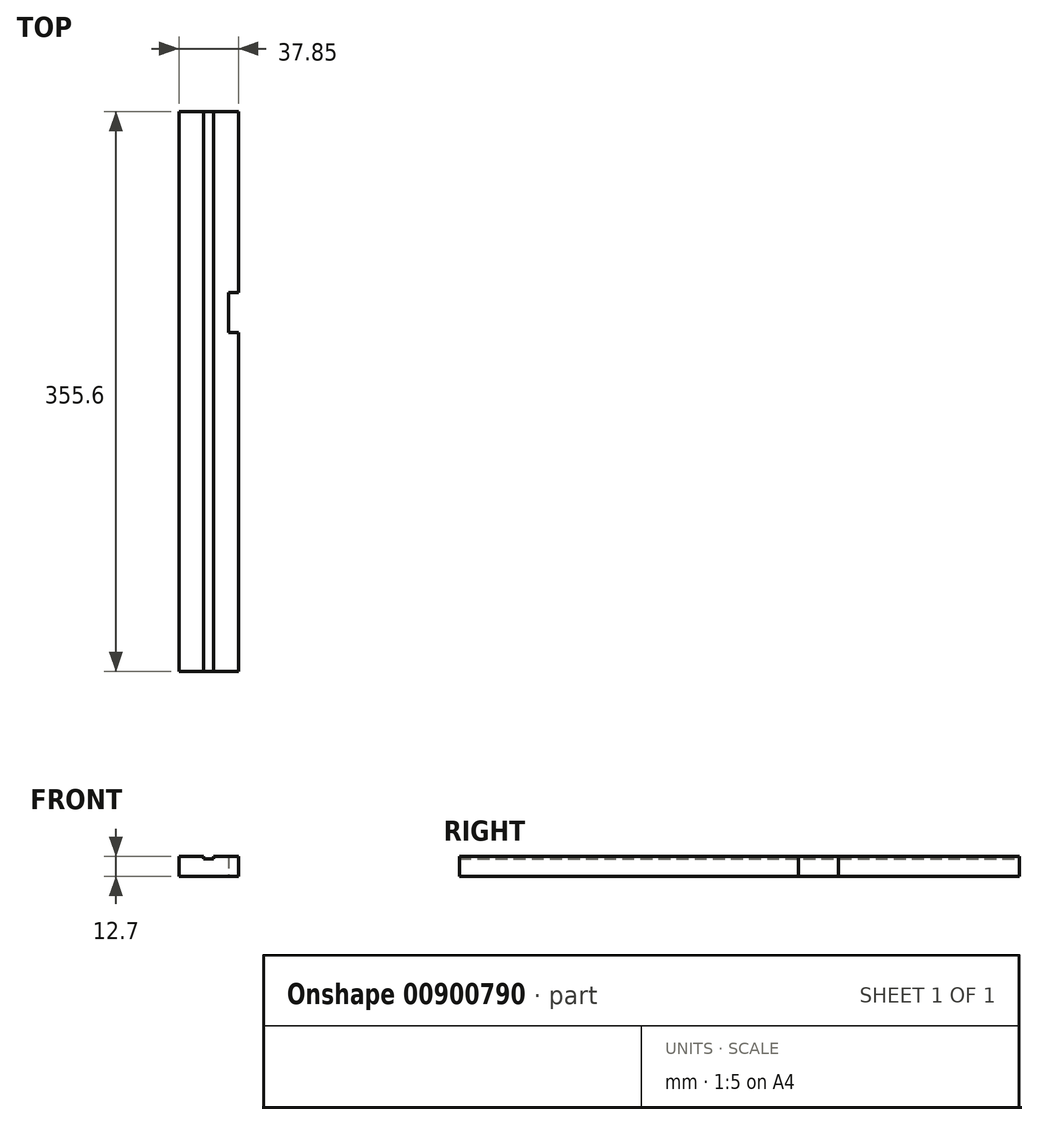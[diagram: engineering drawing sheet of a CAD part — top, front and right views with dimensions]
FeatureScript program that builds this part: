
annotation { "Feature Type Name" : "Feature", "Feature Type Description" : "" }
export const myFeature = defineFeature(function(context is Context, id is Id, definition is map)
    precondition{}
    {
        {
            var Q0;
            Q0=qCreatedBy(makeId("Front.planeOp"),FACE);
            var sketch = newSketch(context, id + "F0", { "sketchPlane" : qUnion([Q0])});
            skLineSegment(sketch, "E0.bottom", {"start": v(0, 12.7) * mm, "end": v(15.75, 12.7) * mm});
            skLineSegment(sketch, "E0.top", {"start": v(0, 0) * mm, "end": v(37.85, 0) * mm});
            skLineSegment(sketch, "E0.left", {"start": v(0, 12.7) * mm, "end": v(0, 0) * mm});
            skLineSegment(sketch, "E0.right", {"start": v(37.85, 12.7) * mm, "end": v(37.85, 0) * mm});
            skLineSegment(sketch, "E1.top", {"start": v(15.75, 11.18) * mm, "end": v(22.1, 11.18) * mm});
            skLineSegment(sketch, "E1.left", {"start": v(15.75, 12.7) * mm, "end": v(15.75, 11.18) * mm});
            skLineSegment(sketch, "E1.right", {"start": v(22.1, 12.7) * mm, "end": v(22.1, 11.18) * mm});
            skLineSegment(sketch, "E2.trimOffspring", {"start": v(22.1, 12.7) * mm, "end": v(37.85, 12.7) * mm});
            skSolve(sketch);
        }
        {
            var Q0;
            Q0=makeQuery(id+"F0.imprint","IMPRINT",FACE,{"disambiguationData":[TD([[makeQuery(id+"F0.imprint","IMPRINT",EDGE,{"derivedFrom":sQuery(id+"F0.wireOp",EDGE,"E0.bottom")}),-1.0]])]});
            extrude(context, id + "F1", {"entities" : qUnion([Q0]), "depth" : 355.6 * mm, "offsetDistance" : 25.4 * mm});
        }
        {
            var Q0;
            Q0=makeQuery(id+"F1.opExtrude","SWEPT_FACE",FACE,{"disambiguationData":[OSD([sQuery(id+"F0.wireOp",EDGE,"E0.right")])]});
            var sketch = newSketch(context, id + "F2", { "sketchPlane" : qUnion([Q0])});
            skLineSegment(sketch, "E3.bottom", {"start": v(-140.2, 37.41) * mm, "end": v(-114.8, 37.41) * mm});
            skLineSegment(sketch, "E3.top", {"start": v(-140.2, -5.95) * mm, "end": v(-114.8, -5.95) * mm});
            skLineSegment(sketch, "E3.left", {"start": v(-140.2, 37.41) * mm, "end": v(-140.2, -5.95) * mm});
            skLineSegment(sketch, "E3.right", {"start": v(-114.8, 37.41) * mm, "end": v(-114.8, -5.95) * mm});
            skSolve(sketch);
        }
        {
            var Q0;
            {var subQ0=sQuery(id+"F2.wireOp",EDGE,"E3.left");var subQ1=sQuery(id+"F0.wireOp",EDGE,"E0.right");var subQ2=makeQuery(id+"F1.opExtrude","SWEPT_EDGE",EDGE,{"disambiguationData":[OSD([subQ1,sQuery(id+"F0.wireOp",EDGE,"E2.trimOffspring")])]});var subQ3=makeQuery(id+"F2.imprint","INTERSECT",VERTEX,{"derivedFrom":[subQ2,subQ0]});Q0=makeQuery(id+"F2.imprint","IMPRINT",FACE,{"disambiguationData":[TD([[makeQuery(id+"F2.imprint","IMPRINT",EDGE,{"disambiguationData":[TD([[subQ3,-1.0]])],"derivedFrom":subQ0}),1.0]])]});}
            extrude(context, id + "F3", {"entities" : qUnion([Q0]), "operationType" : NewBodyOperationType.REMOVE, "oppositeDirection" : true, "depth" : 6.35 * mm, "offsetDistance" : 25.4 * mm});
        }
        {
            var Q0;
            Q0=qCreatedBy(makeId("Right.planeOp"),FACE);
            cPlane(context, id + "F4", {"entities" : qUnion([Q0]), "cplaneType" : CPlaneType.OFFSET, "offset" : 19.05 * mm, "width" : 152.4 * mm, "height" : 152.4 * mm});
        }
    });
